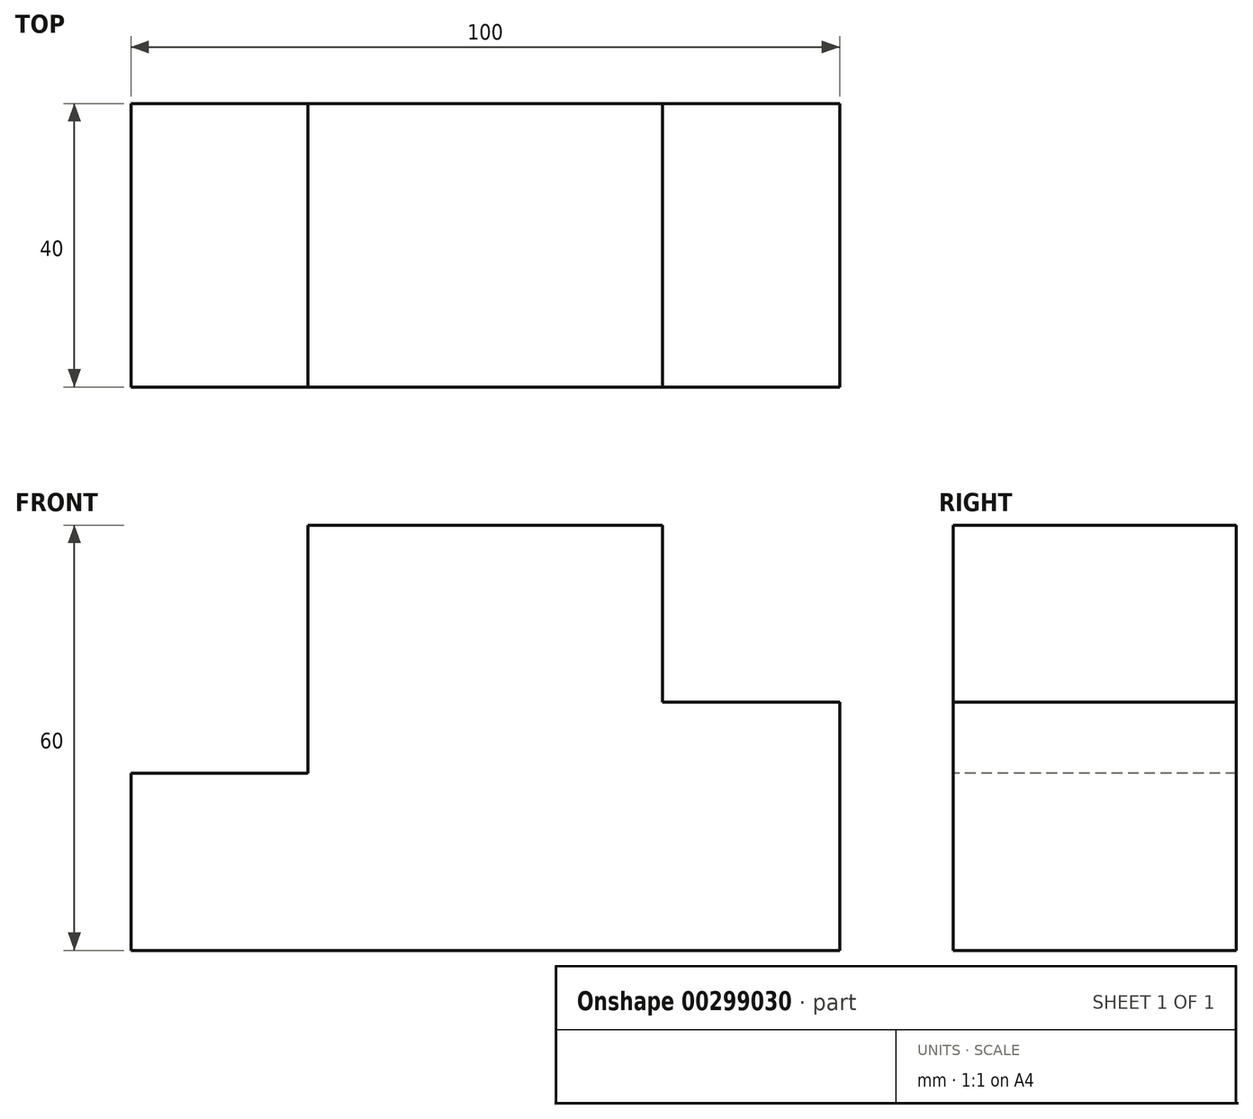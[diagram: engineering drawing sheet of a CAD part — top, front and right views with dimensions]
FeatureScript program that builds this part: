
annotation { "Feature Type Name" : "Feature", "Feature Type Description" : "" }
export const myFeature = defineFeature(function(context is Context, id is Id, definition is map)
    precondition{}
    {
        {
            var Q0;
            Q0=qCreatedBy(makeId("Front.planeOp"),FACE);
            var sketch = newSketch(context, id + "F0", { "sketchPlane" : qUnion([Q0])});
            skLineSegment(sketch, "E0.bottom", {"start": v(-51.95, 12.5) * mm, "end": v(48.05, 12.5) * mm});
            skLineSegment(sketch, "E0.top", {"start": v(-51.95, -12.5) * mm, "end": v(48.05, -12.5) * mm});
            skLineSegment(sketch, "E0.left", {"start": v(-51.95, 12.5) * mm, "end": v(-51.95, -12.5) * mm});
            skLineSegment(sketch, "E0.right", {"start": v(48.05, 12.5) * mm, "end": v(48.05, -12.5) * mm});
            skPoint(sketch, "E0.middle", {"position": v(-1.95, 0) * mm});
            skSolve(sketch);
        }
        {
            var Q0;
            Q0=makeQuery(id+"F0.imprint","IMPRINT",FACE,{"disambiguationData":[TD([[makeQuery(id+"F0.imprint","IMPRINT",EDGE,{"derivedFrom":sQuery(id+"F0.wireOp",EDGE,"E0.bottom")}),-1.0]])]});
            extrude(context, id + "F1", {"entities" : qUnion([Q0]), "depth" : 40 * mm});
        }
        {
            var Q0;
            Q0=makeQuery(id+"F1.opExtrude","SWEPT_FACE",FACE,{"disambiguationData":[OSD([sQuery(id+"F0.wireOp",EDGE,"E0.bottom")])]});
            var sketch = newSketch(context, id + "F2", { "sketchPlane" : qUnion([Q0])});
            skLineSegment(sketch, "E1.bottom", {"start": v(48.05, 0) * mm, "end": v(23.05, 0) * mm});
            skLineSegment(sketch, "E1.top", {"start": v(48.05, -40) * mm, "end": v(23.05, -40) * mm});
            skLineSegment(sketch, "E1.left", {"start": v(48.05, 0) * mm, "end": v(48.05, -40) * mm});
            skLineSegment(sketch, "E1.right", {"start": v(23.05, 0) * mm, "end": v(23.05, -40) * mm});
            skLineSegment(sketch, "E2.bottom", {"start": v(23.05, 0) * mm, "end": v(-26.95, 0) * mm});
            skLineSegment(sketch, "E2.top", {"start": v(23.05, -40) * mm, "end": v(-26.95, -40) * mm});
            skLineSegment(sketch, "E2.right", {"start": v(-26.95, 0) * mm, "end": v(-26.95, -40) * mm});
            skSolve(sketch);
        }
        {
            var Q0;
            Q0=makeQuery(id+"F2.imprint","IMPRINT",FACE,{"disambiguationData":[TD([[makeQuery(id+"F2.imprint","IMPRINT",EDGE,{"derivedFrom":sQuery(id+"F2.wireOp",EDGE,"E1.bottom")}),-1.0]])]});
            extrude(context, id + "F3", {"entities" : qUnion([Q0]), "operationType" : NewBodyOperationType.ADD, "depth" : 10 * mm});
        }
        {
            var Q0;
            Q0=makeQuery(id+"F2.imprint","IMPRINT",FACE,{"disambiguationData":[TD([[makeQuery(id+"F2.imprint","IMPRINT",EDGE,{"derivedFrom":sQuery(id+"F2.wireOp",EDGE,"E2.bottom")}),-1.0]])]});
            extrude(context, id + "F4", {"entities" : qUnion([Q0]), "operationType" : NewBodyOperationType.ADD, "depth" : 35 * mm});
        }
    });
